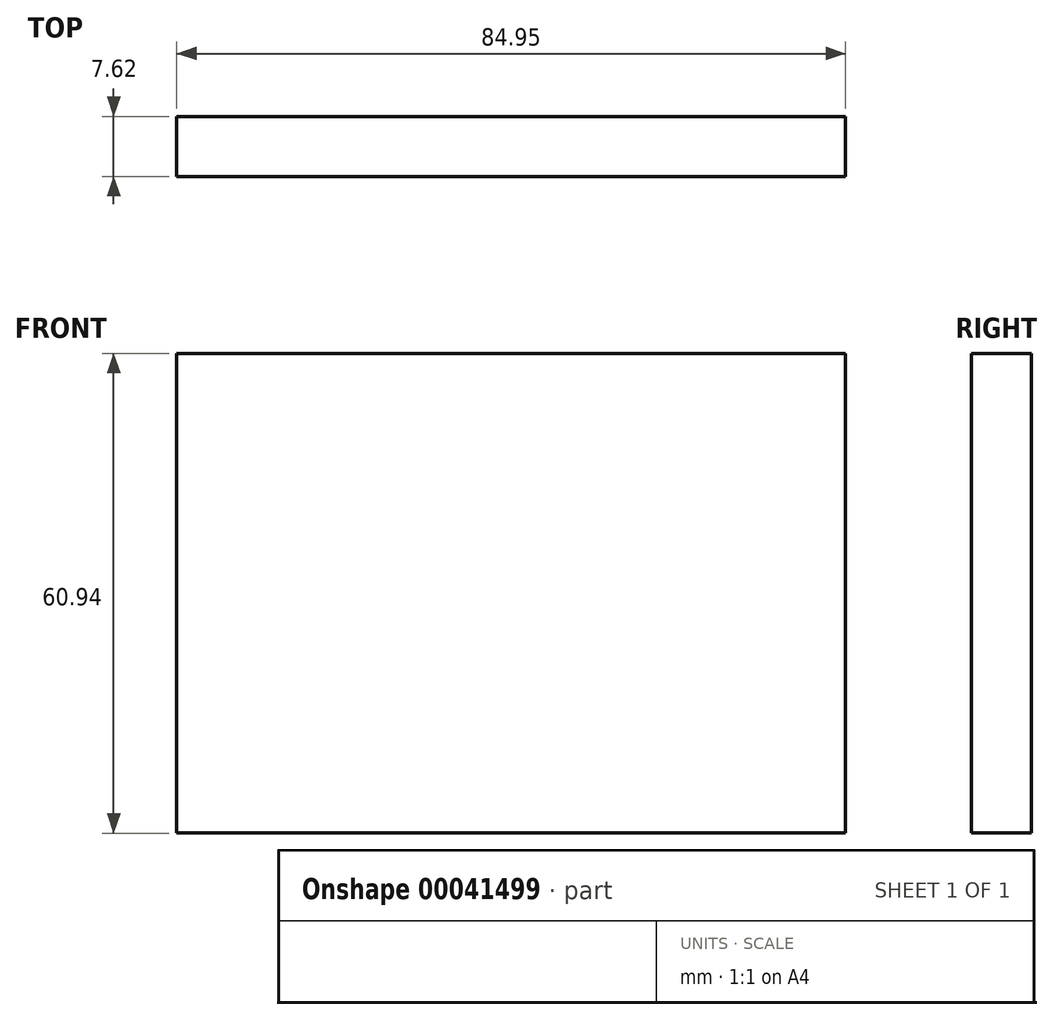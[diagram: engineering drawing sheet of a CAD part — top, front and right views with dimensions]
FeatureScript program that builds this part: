
annotation { "Feature Type Name" : "Feature", "Feature Type Description" : "" }
export const myFeature = defineFeature(function(context is Context, id is Id, definition is map)
    precondition{}
    {
        {
            var Q0;
            Q0=qCreatedBy(makeId("Front.planeOp"),FACE);
            var sketch = newSketch(context, id + "F0", { "sketchPlane" : qUnion([Q0])});
            skLineSegment(sketch, "E0.bottom", {"start": v(42.98, 29.76) * mm, "end": v(-41.97, 29.76) * mm});
            skLineSegment(sketch, "E0.top", {"start": v(42.98, -31.18) * mm, "end": v(-41.97, -31.18) * mm});
            skLineSegment(sketch, "E0.left", {"start": v(42.98, 29.76) * mm, "end": v(42.98, -31.18) * mm});
            skLineSegment(sketch, "E0.right", {"start": v(-41.97, 29.76) * mm, "end": v(-41.97, -31.18) * mm});
            skSolve(sketch);
        }
        {
            var Q0;
            Q0=makeQuery(id+"F0.imprint","IMPRINT",FACE,{"disambiguationData":[TD([[makeQuery(id+"F0.imprint","IMPRINT",EDGE,{"derivedFrom":sQuery(id+"F0.wireOp",EDGE,"E0.bottom")}),1.0]])]});
            extrude(context, id + "F1", {"entities" : qUnion([Q0]), "depth" : 7.62 * mm});
        }
    });
